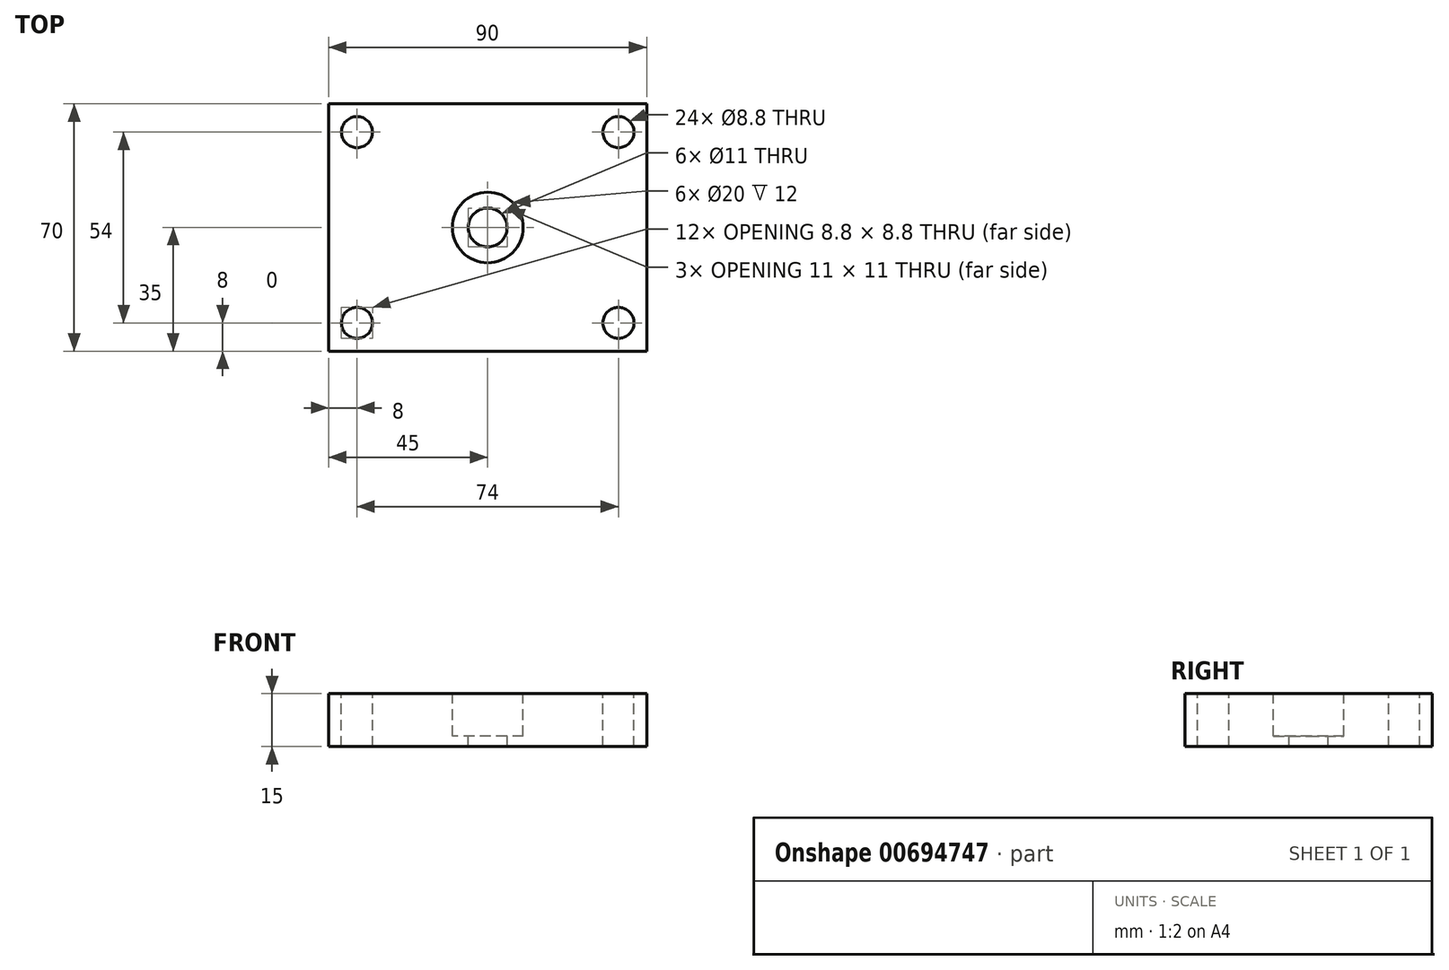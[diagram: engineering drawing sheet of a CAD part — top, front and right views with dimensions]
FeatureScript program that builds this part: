
annotation { "Feature Type Name" : "Feature", "Feature Type Description" : "" }
export const myFeature = defineFeature(function(context is Context, id is Id, definition is map)
    precondition{}
    {
        {
            var Q0;
            Q0=qCreatedBy(makeId("Front.planeOp"),FACE);
            var sketch = newSketch(context, id + "F0", { "sketchPlane" : qUnion([Q0])});
            skLineSegment(sketch, "E0.bottom", {"start": v(0, 0) * mm, "end": v(90, 0) * mm});
            skLineSegment(sketch, "E0.top", {"start": v(0, 15) * mm, "end": v(90, 15) * mm});
            skLineSegment(sketch, "E0.left", {"start": v(0, 0) * mm, "end": v(0, 15) * mm});
            skLineSegment(sketch, "E0.right", {"start": v(90, 0) * mm, "end": v(90, 15) * mm});
            skSolve(sketch);
        }
        {
            var Q0;
            Q0=qCreatedBy(makeId("Right.planeOp"),FACE);
            var sketch = newSketch(context, id + "F1", { "sketchPlane" : qUnion([Q0])});
            skLineSegment(sketch, "E1", {"start": v(0, 0) * mm, "end": v(70, 0) * mm});
            skSolve(sketch);
        }
        {
            var Q0;
            Q0=makeQuery(id+"F0.imprint","IMPRINT",FACE,{"disambiguationData":[TD([[makeQuery(id+"F0.imprint","IMPRINT",EDGE,{"derivedFrom":sQuery(id+"F0.wireOp",EDGE,"E0.bottom")}),1.0]])]});
            var Q1;
            Q1=sQuery(id+"F1.wireOp",EDGE,"E1");
            sweep(context, id + "F2", {"profiles" : qUnion([Q0]), "path" : qUnion([Q1])});
        }
        {
            var Q0;
            Q0=makeQuery(id+"F2.opSweep","SWEPT_FACE",FACE,{"disambiguationData":[OSD([sQuery(id+"F0.wireOp",EDGE,"E0.top"),sQuery(id+"F1.wireOp",EDGE,"E1")])]});
            var sketch = newSketch(context, id + "F3", { "sketchPlane" : qUnion([Q0])});
            skPoint(sketch, "E2", {"position": v(45, 35) * mm});
            skCircle(sketch, "E3", {"center": v(45, 35) * mm, "radius": 35 * mm});
            skPoint(sketch, "E4", {"position": v(8, 62) * mm});
            skPoint(sketch, "E5", {"position": v(8, 8) * mm});
            skCircle(sketch, "E6", {"center": v(8, 62) * mm, "radius": 6.5 * mm});
            skPoint(sketch, "E7", {"position": v(82, 62) * mm});
            skPoint(sketch, "E8", {"position": v(82, 8) * mm});
            skSolve(sketch);
        }
        {
            var Q0;
            Q0=sQuery(id+"F3.wireOp",VERTEX,"E4");
            var Q1;
            Q1=sQuery(id+"F3.wireOp",VERTEX,"E7");
            var Q2;
            Q2=sQuery(id+"F3.wireOp",VERTEX,"E8");
            var Q3;
            Q3=sQuery(id+"F3.wireOp",VERTEX,"E5");
            var Q4;
            Q4=makeQuery(id+"F2.opSweep","SWEPT_BODY",BODY,{"disambiguationData":[OSD([sQuery(id+"F0.wireOp",EDGE,"E0.bottom"),sQuery(id+"F0.wireOp",EDGE,"E0.top"),sQuery(id+"F0.wireOp",EDGE,"E0.left"),sQuery(id+"F0.wireOp",EDGE,"E0.right"),sQuery(id+"F1.wireOp",EDGE,"E1")])]});
            hole(context, id + "F4", {"style" : HoleStyle.SIMPLE, "endStyle" : HoleEndStyle.THROUGH, "standardTappedOrClearance" : lookupTablePath({ "standard" : "ISO", "fit" : "Normal", "size" : "M8", "type" : "Clearance" }), "standardBlindInLast" : lookupTablePath({ "fit" : "Standard", "standard" : "ISO", "size" : "M8", "type" : "Clearance" }), "holeDiameter" : 8.8 * mm, "majorDiameter" : 5 * mm, "isTappedThrough" : true, "tappedDepth" : 12 * mm, "tapClearance" : 3, "locations" : qUnion([Q0, Q1, Q2, Q3]), "scope" : qUnion([Q4])});
        }
        {
            var Q0;
            Q0=makeQuery(id+"F2.opSweep","SWEPT_FACE",FACE,{"disambiguationData":[OSD([sQuery(id+"F0.wireOp",EDGE,"E0.top"),sQuery(id+"F1.wireOp",EDGE,"E1")])]});
            var sketch = newSketch(context, id + "F5", { "sketchPlane" : qUnion([Q0])});
            skPoint(sketch, "E9", {"position": v(45, 35) * mm});
            skSolve(sketch);
        }
        {
            var Q0;
            Q0=sQuery(id+"F5.wireOp",VERTEX,"E9");
            var Q1;
            Q1=makeQuery(id+"F2.opSweep","SWEPT_BODY",BODY,{"disambiguationData":[OSD([sQuery(id+"F0.wireOp",EDGE,"E0.bottom"),sQuery(id+"F0.wireOp",EDGE,"E0.top"),sQuery(id+"F0.wireOp",EDGE,"E0.left"),sQuery(id+"F0.wireOp",EDGE,"E0.right"),sQuery(id+"F1.wireOp",EDGE,"E1")])]});
            hole(context, id + "F6", {"style" : HoleStyle.C_BORE, "endStyle" : HoleEndStyle.THROUGH, "holeDiameter" : 11 * mm, "cBoreDiameter" : 20 * mm, "cBoreDepth" : 12 * mm, "majorDiameter" : 5 * mm, "isTappedThrough" : true, "tappedDepth" : 12 * mm, "tapClearance" : 3, "locations" : qUnion([Q0]), "scope" : qUnion([Q1])});
        }
    });
